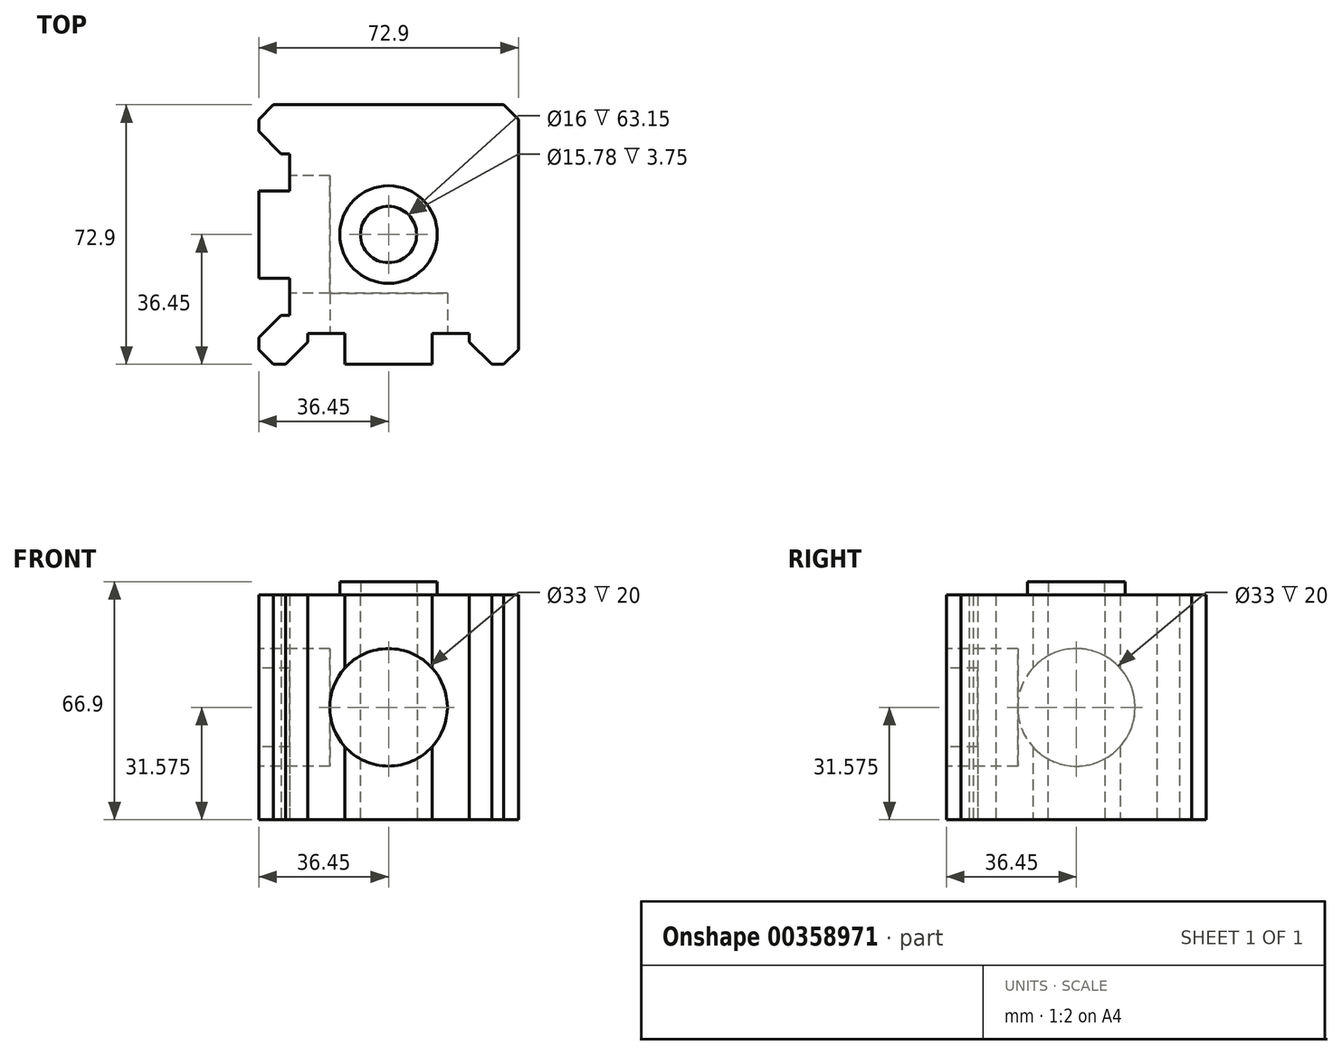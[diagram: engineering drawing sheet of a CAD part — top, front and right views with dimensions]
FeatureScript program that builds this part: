
annotation { "Feature Type Name" : "Feature", "Feature Type Description" : "" }
export const myFeature = defineFeature(function(context is Context, id is Id, definition is map)
    precondition{}
    {
        {
            var Q0;
            Q0=qCreatedBy(makeId("Top.planeOp"),FACE);
            var sketch = newSketch(context, id + "F0", { "sketchPlane" : qUnion([Q0])});
            skLineSegment(sketch, "E0.bottom", {"start": v(-32.35, 36.45) * mm, "end": v(32.35, 36.45) * mm});
            skLineSegment(sketch, "E0.top", {"start": v(-32.35, -36.45) * mm, "end": v(-28.95, -36.45) * mm});
            skLineSegment(sketch, "E0.right", {"start": v(36.45, 32.35) * mm, "end": v(36.45, -32.35) * mm});
            skCircle(sketch, "E1", {"center": v(0, 0) * mm, "radius": 8 * mm});
            skLineSegment(sketch, "E2", {"start": v(36.45, -32.35) * mm, "end": v(32.35, -36.45) * mm});
            skLineSegment(sketch, "E3", {"start": v(36.45, 36.45) * mm, "end": v(-34.4, -34.4) * mm, "construction": true});
            skLineSegment(sketch, "E4.MirrorCS", {"start": v(36.45, 32.35) * mm, "end": v(32.35, 36.45) * mm});
            skLineSegment(sketch, "E5.MirrorCS", {"start": v(-36.45, -32.35) * mm, "end": v(-32.35, -36.45) * mm});
            skLineSegment(sketch, "E6.MirrorCS", {"start": v(-36.45, 32.35) * mm, "end": v(-32.35, 36.45) * mm});
            skLineSegment(sketch, "E7", {"start": v(28.95, -36.45) * mm, "end": v(22.65, -30.15) * mm});
            skLineSegment(sketch, "E8", {"start": v(22.65, -27.75) * mm, "end": v(12.25, -27.75) * mm});
            skLineSegment(sketch, "E9", {"start": v(22.65, -30.15) * mm, "end": v(22.65, -27.75) * mm});
            skLineSegment(sketch, "E10", {"start": v(12.25, -27.75) * mm, "end": v(12.25, -36.45) * mm});
            skLineSegment(sketch, "E11.trimOffspring", {"start": v(28.95, -36.45) * mm, "end": v(32.35, -36.45) * mm});
            skLineSegment(sketch, "E12.MirrorCS", {"start": v(-43.95, -43.95) * mm, "end": v(28.95, 28.95) * mm, "construction": true});
            skLineSegment(sketch, "E13.MirrorCS", {"start": v(-36.45, 28.95) * mm, "end": v(-30.15, 22.65) * mm});
            skLineSegment(sketch, "E14.MirrorCS", {"start": v(-30.15, 22.65) * mm, "end": v(-27.75, 22.65) * mm});
            skLineSegment(sketch, "E15.MirrorCS", {"start": v(-27.75, 22.65) * mm, "end": v(-27.75, 12.25) * mm});
            skLineSegment(sketch, "E16.MirrorCS", {"start": v(-27.75, 12.25) * mm, "end": v(-36.45, 12.25) * mm});
            skLineSegment(sketch, "E17.MirrorCS", {"start": v(-12.25, -27.75) * mm, "end": v(-12.25, -36.45) * mm});
            skLineSegment(sketch, "E18.MirrorCS", {"start": v(-22.65, -27.75) * mm, "end": v(-12.25, -27.75) * mm});
            skLineSegment(sketch, "E19.MirrorCS", {"start": v(-22.65, -30.15) * mm, "end": v(-22.65, -27.75) * mm});
            skLineSegment(sketch, "E20.MirrorCS", {"start": v(-28.95, -36.45) * mm, "end": v(-22.65, -30.15) * mm});
            skLineSegment(sketch, "E21.MirrorCS", {"start": v(-36.45, -28.95) * mm, "end": v(-30.15, -22.65) * mm});
            skLineSegment(sketch, "E22.MirrorCS", {"start": v(-30.15, -22.65) * mm, "end": v(-27.75, -22.65) * mm});
            skLineSegment(sketch, "E23.MirrorCS", {"start": v(-27.75, -22.65) * mm, "end": v(-27.75, -12.25) * mm});
            skLineSegment(sketch, "E24.MirrorCS", {"start": v(-27.75, -12.25) * mm, "end": v(-36.45, -12.25) * mm});
            skLineSegment(sketch, "E25.trimOffspring", {"start": v(-36.45, 12.25) * mm, "end": v(-36.45, -12.25) * mm});
            skLineSegment(sketch, "E26.trimOffspring", {"start": v(-12.25, -36.45) * mm, "end": v(12.25, -36.45) * mm});
            skPoint(sketch, "E27.orphan", {"position": v(-36.45, -36.45) * mm});
            skLineSegment(sketch, "E28", {"start": v(-36.45, 28.95) * mm, "end": v(-36.45, 32.35) * mm});
            skLineSegment(sketch, "E29", {"start": v(-36.45, -28.95) * mm, "end": v(-36.45, -32.35) * mm});
            skSolve(sketch);
        }
        {
            var Q0;
            Q0 = qSketchRegion(id + "F0", true);
            extrude(context, id + "F1", {"entities" : qUnion([Q0]), "depth" : 63.15 * mm});
        }
        {
            var Q0;
            Q0=makeQuery(id+"F1.opExtrude","SWEPT_FACE",FACE,{"disambiguationData":[OSD([sQuery(id+"F0.wireOp",EDGE,"E26.trimOffspring")])]});
            var sketch = newSketch(context, id + "F2", { "sketchPlane" : qUnion([Q0])});
            skCircle(sketch, "E30", {"center": v(0, 31.57) * mm, "radius": 16.5 * mm});
            skPoint(sketch, "E30.centerSnap0", {"position": v(-12.25, 31.57) * mm});
            skSolve(sketch);
        }
        {
            var Q0;
            Q0 = qSketchRegion(id + "F2", true);
            extrude(context, id + "F3", {"entities" : qUnion([Q0]), "operationType" : NewBodyOperationType.REMOVE, "oppositeDirection" : true, "depth" : 20 * mm});
        }
        {
            var Q0;
            Q0=makeQuery(id+"F1.opExtrude","SWEPT_FACE",FACE,{"disambiguationData":[OSD([sQuery(id+"F0.wireOp",EDGE,"E25.trimOffspring")])]});
            var sketch = newSketch(context, id + "F4", { "sketchPlane" : qUnion([Q0])});
            skCircle(sketch, "E31", {"center": v(0, 31.57) * mm, "radius": 16.5 * mm});
            skPoint(sketch, "E31.centerSnap0", {"position": v(-12.25, 31.57) * mm});
            skSolve(sketch);
        }
        {
            var Q0;
            Q0 = qSketchRegion(id + "F4", true);
            extrude(context, id + "F5", {"entities" : qUnion([Q0]), "operationType" : NewBodyOperationType.REMOVE, "oppositeDirection" : true, "depth" : 20 * mm});
        }
        {
            var Q0;
            Q0=makeQuery(id+"F1.opExtrude","CAP_FACE",FACE,{"disambiguationData":[OSD([sQuery(id+"F0.wireOp",EDGE,"E0.bottom"),sQuery(id+"F0.wireOp",EDGE,"E0.top"),sQuery(id+"F0.wireOp",EDGE,"E0.right"),sQuery(id+"F0.wireOp",EDGE,"E1"),sQuery(id+"F0.wireOp",EDGE,"E2"),sQuery(id+"F0.wireOp",EDGE,"E4.MirrorCS"),sQuery(id+"F0.wireOp",EDGE,"E5.MirrorCS"),sQuery(id+"F0.wireOp",EDGE,"E6.MirrorCS"),sQuery(id+"F0.wireOp",EDGE,"E7"),sQuery(id+"F0.wireOp",EDGE,"E8"),sQuery(id+"F0.wireOp",EDGE,"E9"),sQuery(id+"F0.wireOp",EDGE,"E10"),sQuery(id+"F0.wireOp",EDGE,"E11.trimOffspring"),sQuery(id+"F0.wireOp",EDGE,"E13.MirrorCS"),sQuery(id+"F0.wireOp",EDGE,"E14.MirrorCS"),sQuery(id+"F0.wireOp",EDGE,"E15.MirrorCS"),sQuery(id+"F0.wireOp",EDGE,"E16.MirrorCS"),sQuery(id+"F0.wireOp",EDGE,"E17.MirrorCS"),sQuery(id+"F0.wireOp",EDGE,"E18.MirrorCS"),sQuery(id+"F0.wireOp",EDGE,"E19.MirrorCS"),sQuery(id+"F0.wireOp",EDGE,"E20.MirrorCS"),sQuery(id+"F0.wireOp",EDGE,"E21.MirrorCS"),sQuery(id+"F0.wireOp",EDGE,"E22.MirrorCS"),sQuery(id+"F0.wireOp",EDGE,"E23.MirrorCS"),sQuery(id+"F0.wireOp",EDGE,"E24.MirrorCS"),sQuery(id+"F0.wireOp",EDGE,"E25.trimOffspring"),sQuery(id+"F0.wireOp",EDGE,"E26.trimOffspring"),sQuery(id+"F0.wireOp",EDGE,"E28"),sQuery(id+"F0.wireOp",EDGE,"E29")])],"isStart":false});
            var sketch = newSketch(context, id + "F6", { "sketchPlane" : qUnion([Q0])});
            skCircle(sketch, "E32", {"center": v(0, 0) * mm, "radius": 13.7 * mm});
            skCircle(sketch, "E33", {"center": v(0, 0) * mm, "radius": 7.89 * mm});
            skSolve(sketch);
        }
        {
            var Q0;
            Q0 = qSketchRegion(id + "F6", true);
            extrude(context, id + "F7", {"entities" : qUnion([Q0]), "operationType" : NewBodyOperationType.ADD, "depth" : 3.75 * mm});
        }
    });
